# Revit family: V62A-42U-With doors-08.04.14
name_source: partatom
category: Electrical Equipment
revit_build: Autodesk Revit 2013 (Build: 20130531_2115(x64)
units: mm (PartAtom-declared; Revit-internal decimal feet)

## types (1)
- V62A-42U
    Cabinet Depth = 1200 mm
    Cabinet Height = 2016 mm  [stored 6.61417 ft]
    Cabinet Width Overall = 600 mm
    Color = BLACK
    Description = WARNING: PLEASE RELOAD FAMILY USING THE TYPE CATALOG
    Door Back = Yes
    Door Construction Side = 2
    Door Front = Yes
    Item Class = 1F
    Item Group = RACKS
    Manufacturer = SIEMON
    Metal = SIEMON STEEL
    Model = V62A
    Mounting Rail Material = SIEMON STEEL
    Mounting rail 45 U = SIEMON STEEL
    Ports = 0
    Segment = CSS
    Side Panel Left = Yes
    Side Panel Right = Yes
    System = VPOD
    U Space = 42
    U/M = EA
    Usable Depth = 1006 mm  [stored 3.30052 ft]
    Weight = 0.00 lb

note: [stored X ft] marks values corroborated as IEEE doubles in the binary element streams (Revit-internal decimal feet)

## geometry (parser evidence)
native form markers: Blend x16, Sweep x16
no freeform markers — native parametric forms only
